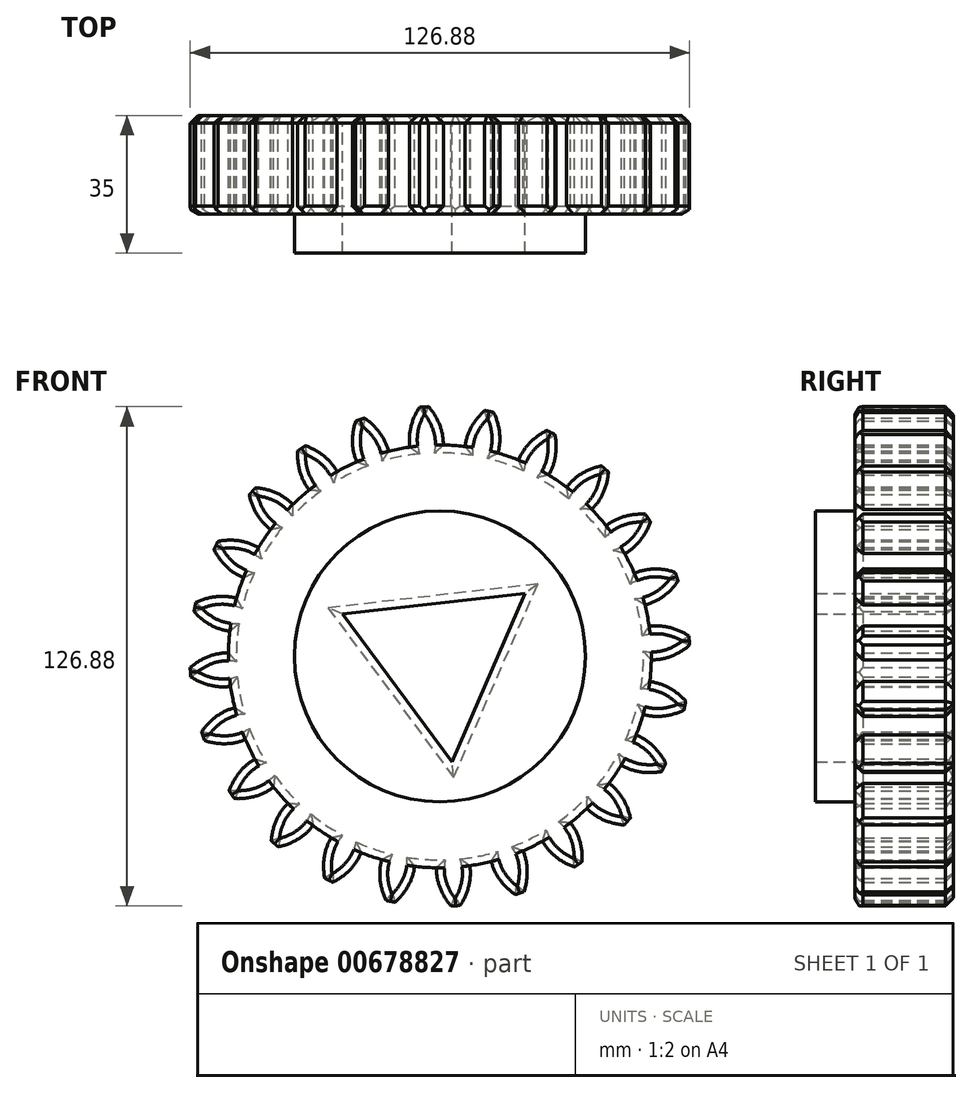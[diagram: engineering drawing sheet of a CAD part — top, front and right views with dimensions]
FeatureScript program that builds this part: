
annotation { "Feature Type Name" : "Feature", "Feature Type Description" : "" }
export const myFeature = defineFeature(function(context is Context, id is Id, definition is map)
    precondition{}
    {
        {
            var Q0;
            Q0=qCreatedBy(makeId("Front.planeOp"),FACE);
            var sketch = newSketch(context, id + "F0", { "sketchPlane" : qUnion([Q0])});
            skCircle(sketch, "E0", {"center": v(0, 0) * mm, "radius": 53.72 * mm});
            skCircle(sketch, "E1", {"center": v(0, 0) * mm, "radius": 58.67 * mm, "construction": true});
            skCircle(sketch, "E2", {"center": v(0, 0) * mm, "radius": 63.5 * mm, "construction": true});
            skLineSegment(sketch, "E3", {"start": v(0, 0) * mm, "end": v(0, 76.25) * mm, "construction": true});
            skLineSegment(sketch, "E4", {"start": v(0, 2.12) * mm, "end": v(-4.61, 72.47) * mm, "construction": true});
            skLineSegment(sketch, "E5", {"start": v(0, 58.67) * mm, "end": v(-65.77, 58.67) * mm, "construction": true});
            skLineSegment(sketch, "E6", {"start": v(0, 58.67) * mm, "end": v(-63.3, 35.64) * mm, "construction": true});
            skCircle(sketch, "E7", {"center": v(0, 58.67) * mm, "radius": 14.6 * mm, "construction": true});
            skCircle(sketch, "E8", {"center": v(-13.72, 53.68) * mm, "radius": 14.6 * mm, "construction": true});
            skArc(sketch, "E9", {"start": v(0, 58.67) * mm, "mid": v(-1.22, 61.18) * mm, "end": v(-2.86, 63.44) * mm});
            skArc(sketch, "E10", {"start": v(0.88, 53.71) * mm, "mid": v(0.68, 56.24) * mm, "end": v(0, 58.67) * mm});
            skArc(sketch, "E11.MirrorCS", {"start": v(-7.38, 58.2) * mm, "mid": v(-6.5, 60.83) * mm, "end": v(-5.17, 63.28) * mm});
            skArc(sketch, "E12.MirrorCS", {"start": v(-7.6, 53.16) * mm, "mid": v(-7.73, 55.68) * mm, "end": v(-7.38, 58.2) * mm});
            skLineSegment(sketch, "E13", {"start": v(-5.17, 63.28) * mm, "end": v(-2.86, 63.44) * mm});
            skCircle(sketch, "E14", {"center": v(0, 0) * mm, "radius": 55.14 * mm, "construction": true});
            skCircle(sketch, "E15", {"center": v(0, 0) * mm, "radius": 36.96 * mm});
            skCircle(sketch, "E16.cCircle", {"center": v(0, 0) * mm, "radius": 26.94 * mm, "construction": true});
            skLineSegment(sketch, "E16.0", {"start": v(3.04, -26.76) * mm, "end": v(-24.7, 10.75) * mm});
            skLineSegment(sketch, "E16.1", {"start": v(-24.7, 10.75) * mm, "end": v(21.66, 16.02) * mm});
            skLineSegment(sketch, "E16.2", {"start": v(21.66, 16.02) * mm, "end": v(3.04, -26.76) * mm});
            skSolve(sketch);
        }
        {
            var Q0;
            {var subQ0=sQuery(id+"F0.wireOp",EDGE,"E0");var subQ1=makeQuery(id+"F0.imprint","INTERSECT",VERTEX,{"derivedFrom":[subQ0,sQuery(id+"F0.wireOp",EDGE,"E10")]});Q0=makeQuery(id+"F0.imprint","IMPRINT",FACE,{"disambiguationData":[TD([[makeQuery(id+"F0.imprint","IMPRINT",EDGE,{"disambiguationData":[TD([[subQ1,-1.0]])],"derivedFrom":subQ0}),1.0]])]});}
            var Q1;
            Q1=makeQuery(id+"F0.imprint","IMPRINT",FACE,{"disambiguationData":[TD([[makeQuery(id+"F0.imprint","IMPRINT",EDGE,{"derivedFrom":sQuery(id+"F0.wireOp",EDGE,"E9")}),1.0]])]});
            extrude(context, id + "F1", {"entities" : qUnion([Q0, Q1]), "depth" : 25 * mm, "offsetDistance" : 25 * mm});
        }
        {
            var Q0;
            Q0=makeQuery(id+"F1.opExtrude","SWEPT_BODY",BODY,{"disambiguationData":[OSD([sQuery(id+"F0.wireOp",EDGE,"E0"),sQuery(id+"F0.wireOp",EDGE,"E9"),sQuery(id+"F0.wireOp",EDGE,"E10"),sQuery(id+"F0.wireOp",EDGE,"E11.MirrorCS"),sQuery(id+"F0.wireOp",EDGE,"E12.MirrorCS"),sQuery(id+"F0.wireOp",EDGE,"E13")])]});
            var Q1;
            Q1=makeQuery(id+"F1.opExtrude","SWEPT_FACE",FACE,{"disambiguationData":[OSD([sQuery(id+"F0.wireOp",EDGE,"E0")])]});
            circularPattern(context, id + "F2", {"entities" : qUnion([Q0]), "axis" : qUnion([Q1]), "angle" : 360 * degree, "instanceCount" : 24, "equalSpace" : true});
        }
        {
            var Q0;
            Q0=makeQuery(id+"F0.imprint","IMPRINT",FACE,{"disambiguationData":[TD([[makeQuery(id+"F0.imprint","IMPRINT",EDGE,{"derivedFrom":sQuery(id+"F0.wireOp",EDGE,"E15")}),1.0]])]});
            extrude(context, id + "F3", {"entities" : qUnion([Q0]), "operationType" : NewBodyOperationType.ADD, "depth" : 35 * mm, "offsetDistance" : 25 * mm});
        }
        {
            var Q0;
            Q0=makeQuery(id+"F2.opPattern","COPY",EDGE,{"derivedFrom":makeQuery(id+"F1.opExtrude","CAP_EDGE",EDGE,{"disambiguationData":[OSD([sQuery(id+"F0.wireOp",EDGE,"E10")])],"isStart":false}),"instanceName":"21"});
            var Q1;
            Q1=makeQuery(id+"F2.opPattern","COPY",EDGE,{"derivedFrom":makeQuery(id+"F1.opExtrude","CAP_EDGE",EDGE,{"disambiguationData":[OSD([sQuery(id+"F0.wireOp",EDGE,"E12.MirrorCS")])],"isStart":false}),"instanceName":"22"});
            var Q2;
            Q2=makeQuery(id+"F2.opPattern","COPY",EDGE,{"derivedFrom":makeQuery(id+"F1.opExtrude","CAP_EDGE",EDGE,{"disambiguationData":[OSD([sQuery(id+"F0.wireOp",EDGE,"E12.MirrorCS")])],"isStart":false}),"instanceName":"21"});
            var Q3;
            Q3=makeQuery(id+"F2.opPattern","COPY",EDGE,{"derivedFrom":makeQuery(id+"F1.opExtrude","CAP_EDGE",EDGE,{"disambiguationData":[OSD([sQuery(id+"F0.wireOp",EDGE,"E10")])],"isStart":false}),"instanceName":"22"});
            var Q4;
            Q4=makeQuery(id+"F2.opPattern","COPY",EDGE,{"derivedFrom":makeQuery(id+"F1.opExtrude","CAP_EDGE",EDGE,{"disambiguationData":[OSD([sQuery(id+"F0.wireOp",EDGE,"E12.MirrorCS")])],"isStart":false}),"instanceName":"23"});
            var Q5;
            Q5=makeQuery(id+"F2.opPattern","COPY",EDGE,{"derivedFrom":makeQuery(id+"F1.opExtrude","CAP_EDGE",EDGE,{"disambiguationData":[OSD([sQuery(id+"F0.wireOp",EDGE,"E10")])],"isStart":false}),"instanceName":"23"});
            var Q6;
            Q6=makeQuery(id+"F1.opExtrude","CAP_EDGE",EDGE,{"disambiguationData":[OSD([sQuery(id+"F0.wireOp",EDGE,"E12.MirrorCS")])],"isStart":false});
            var Q7;
            Q7=makeQuery(id+"F1.opExtrude","CAP_EDGE",EDGE,{"disambiguationData":[OSD([sQuery(id+"F0.wireOp",EDGE,"E10")])],"isStart":false});
            var Q8;
            Q8=makeQuery(id+"F2.opPattern","COPY",EDGE,{"derivedFrom":makeQuery(id+"F1.opExtrude","CAP_EDGE",EDGE,{"disambiguationData":[OSD([sQuery(id+"F0.wireOp",EDGE,"E12.MirrorCS")])],"isStart":false}),"instanceName":"1"});
            var Q9;
            Q9=makeQuery(id+"F2.opPattern","COPY",EDGE,{"derivedFrom":makeQuery(id+"F1.opExtrude","CAP_EDGE",EDGE,{"disambiguationData":[OSD([sQuery(id+"F0.wireOp",EDGE,"E10")])],"isStart":false}),"instanceName":"1"});
            var Q10;
            Q10=makeQuery(id+"F2.opPattern","COPY",EDGE,{"derivedFrom":makeQuery(id+"F1.opExtrude","CAP_EDGE",EDGE,{"disambiguationData":[OSD([sQuery(id+"F0.wireOp",EDGE,"E12.MirrorCS")])],"isStart":false}),"instanceName":"2"});
            var Q11;
            Q11=makeQuery(id+"F2.opPattern","COPY",EDGE,{"derivedFrom":makeQuery(id+"F1.opExtrude","CAP_EDGE",EDGE,{"disambiguationData":[OSD([sQuery(id+"F0.wireOp",EDGE,"E10")])],"isStart":false}),"instanceName":"2"});
            var Q12;
            Q12=makeQuery(id+"F2.opPattern","COPY",EDGE,{"derivedFrom":makeQuery(id+"F1.opExtrude","CAP_EDGE",EDGE,{"disambiguationData":[OSD([sQuery(id+"F0.wireOp",EDGE,"E12.MirrorCS")])],"isStart":false}),"instanceName":"3"});
            var Q13;
            Q13=makeQuery(id+"F2.opPattern","COPY",EDGE,{"derivedFrom":makeQuery(id+"F1.opExtrude","CAP_EDGE",EDGE,{"disambiguationData":[OSD([sQuery(id+"F0.wireOp",EDGE,"E10")])],"isStart":false}),"instanceName":"3"});
            var Q14;
            Q14=makeQuery(id+"F2.opPattern","COPY",EDGE,{"derivedFrom":makeQuery(id+"F1.opExtrude","CAP_EDGE",EDGE,{"disambiguationData":[OSD([sQuery(id+"F0.wireOp",EDGE,"E12.MirrorCS")])],"isStart":false}),"instanceName":"4"});
            var Q15;
            Q15=makeQuery(id+"F2.opPattern","COPY",EDGE,{"derivedFrom":makeQuery(id+"F1.opExtrude","CAP_EDGE",EDGE,{"disambiguationData":[OSD([sQuery(id+"F0.wireOp",EDGE,"E10")])],"isStart":false}),"instanceName":"4"});
            var Q16;
            Q16=makeQuery(id+"F2.opPattern","COPY",EDGE,{"derivedFrom":makeQuery(id+"F1.opExtrude","CAP_EDGE",EDGE,{"disambiguationData":[OSD([sQuery(id+"F0.wireOp",EDGE,"E10")])],"isStart":false}),"instanceName":"5"});
            var Q17;
            Q17=makeQuery(id+"F2.opPattern","COPY",EDGE,{"derivedFrom":makeQuery(id+"F1.opExtrude","CAP_EDGE",EDGE,{"disambiguationData":[OSD([sQuery(id+"F0.wireOp",EDGE,"E12.MirrorCS")])],"isStart":false}),"instanceName":"5"});
            var Q18;
            Q18=makeQuery(id+"F2.opPattern","COPY",EDGE,{"derivedFrom":makeQuery(id+"F1.opExtrude","CAP_EDGE",EDGE,{"disambiguationData":[OSD([sQuery(id+"F0.wireOp",EDGE,"E12.MirrorCS")])],"isStart":false}),"instanceName":"6"});
            var Q19;
            Q19=makeQuery(id+"F2.opPattern","COPY",EDGE,{"derivedFrom":makeQuery(id+"F1.opExtrude","CAP_EDGE",EDGE,{"disambiguationData":[OSD([sQuery(id+"F0.wireOp",EDGE,"E10")])],"isStart":false}),"instanceName":"6"});
            var Q20;
            Q20=makeQuery(id+"F2.opPattern","COPY",EDGE,{"derivedFrom":makeQuery(id+"F1.opExtrude","CAP_EDGE",EDGE,{"disambiguationData":[OSD([sQuery(id+"F0.wireOp",EDGE,"E12.MirrorCS")])],"isStart":false}),"instanceName":"7"});
            var Q21;
            Q21=makeQuery(id+"F2.opPattern","COPY",EDGE,{"derivedFrom":makeQuery(id+"F1.opExtrude","CAP_EDGE",EDGE,{"disambiguationData":[OSD([sQuery(id+"F0.wireOp",EDGE,"E10")])],"isStart":false}),"instanceName":"7"});
            var Q22;
            Q22=makeQuery(id+"F2.opPattern","COPY",EDGE,{"derivedFrom":makeQuery(id+"F1.opExtrude","CAP_EDGE",EDGE,{"disambiguationData":[OSD([sQuery(id+"F0.wireOp",EDGE,"E12.MirrorCS")])],"isStart":false}),"instanceName":"8"});
            var Q23;
            Q23=makeQuery(id+"F2.opPattern","COPY",EDGE,{"derivedFrom":makeQuery(id+"F1.opExtrude","CAP_EDGE",EDGE,{"disambiguationData":[OSD([sQuery(id+"F0.wireOp",EDGE,"E10")])],"isStart":false}),"instanceName":"8"});
            var Q24;
            Q24=makeQuery(id+"F2.opPattern","COPY",EDGE,{"derivedFrom":makeQuery(id+"F1.opExtrude","CAP_EDGE",EDGE,{"disambiguationData":[OSD([sQuery(id+"F0.wireOp",EDGE,"E12.MirrorCS")])],"isStart":false}),"instanceName":"9"});
            var Q25;
            Q25=makeQuery(id+"F2.opPattern","COPY",EDGE,{"derivedFrom":makeQuery(id+"F1.opExtrude","CAP_EDGE",EDGE,{"disambiguationData":[OSD([sQuery(id+"F0.wireOp",EDGE,"E10")])],"isStart":false}),"instanceName":"9"});
            var Q26;
            Q26=makeQuery(id+"F2.opPattern","COPY",EDGE,{"derivedFrom":makeQuery(id+"F1.opExtrude","CAP_EDGE",EDGE,{"disambiguationData":[OSD([sQuery(id+"F0.wireOp",EDGE,"E12.MirrorCS")])],"isStart":false}),"instanceName":"10"});
            var Q27;
            Q27=makeQuery(id+"F2.opPattern","COPY",EDGE,{"derivedFrom":makeQuery(id+"F1.opExtrude","CAP_EDGE",EDGE,{"disambiguationData":[OSD([sQuery(id+"F0.wireOp",EDGE,"E10")])],"isStart":false}),"instanceName":"10"});
            var Q28;
            Q28=makeQuery(id+"F2.opPattern","COPY",EDGE,{"derivedFrom":makeQuery(id+"F1.opExtrude","CAP_EDGE",EDGE,{"disambiguationData":[OSD([sQuery(id+"F0.wireOp",EDGE,"E12.MirrorCS")])],"isStart":false}),"instanceName":"11"});
            var Q29;
            Q29=makeQuery(id+"F2.opPattern","COPY",EDGE,{"derivedFrom":makeQuery(id+"F1.opExtrude","CAP_EDGE",EDGE,{"disambiguationData":[OSD([sQuery(id+"F0.wireOp",EDGE,"E10")])],"isStart":false}),"instanceName":"11"});
            var Q30;
            Q30=makeQuery(id+"F2.opPattern","COPY",EDGE,{"derivedFrom":makeQuery(id+"F1.opExtrude","CAP_EDGE",EDGE,{"disambiguationData":[OSD([sQuery(id+"F0.wireOp",EDGE,"E12.MirrorCS")])],"isStart":false}),"instanceName":"12"});
            var Q31;
            Q31=makeQuery(id+"F2.opPattern","COPY",EDGE,{"derivedFrom":makeQuery(id+"F1.opExtrude","CAP_EDGE",EDGE,{"disambiguationData":[OSD([sQuery(id+"F0.wireOp",EDGE,"E10")])],"isStart":false}),"instanceName":"12"});
            var Q32;
            Q32=makeQuery(id+"F2.opPattern","COPY",EDGE,{"derivedFrom":makeQuery(id+"F1.opExtrude","CAP_EDGE",EDGE,{"disambiguationData":[OSD([sQuery(id+"F0.wireOp",EDGE,"E12.MirrorCS")])],"isStart":false}),"instanceName":"13"});
            var Q33;
            Q33=makeQuery(id+"F2.opPattern","COPY",EDGE,{"derivedFrom":makeQuery(id+"F1.opExtrude","CAP_EDGE",EDGE,{"disambiguationData":[OSD([sQuery(id+"F0.wireOp",EDGE,"E10")])],"isStart":false}),"instanceName":"13"});
            var Q34;
            Q34=makeQuery(id+"F2.opPattern","COPY",EDGE,{"derivedFrom":makeQuery(id+"F1.opExtrude","CAP_EDGE",EDGE,{"disambiguationData":[OSD([sQuery(id+"F0.wireOp",EDGE,"E12.MirrorCS")])],"isStart":false}),"instanceName":"14"});
            var Q35;
            Q35=makeQuery(id+"F2.opPattern","COPY",EDGE,{"derivedFrom":makeQuery(id+"F1.opExtrude","CAP_EDGE",EDGE,{"disambiguationData":[OSD([sQuery(id+"F0.wireOp",EDGE,"E10")])],"isStart":false}),"instanceName":"14"});
            var Q36;
            Q36=makeQuery(id+"F2.opPattern","COPY",EDGE,{"derivedFrom":makeQuery(id+"F1.opExtrude","CAP_EDGE",EDGE,{"disambiguationData":[OSD([sQuery(id+"F0.wireOp",EDGE,"E12.MirrorCS")])],"isStart":false}),"instanceName":"15"});
            var Q37;
            Q37=makeQuery(id+"F2.opPattern","COPY",EDGE,{"derivedFrom":makeQuery(id+"F1.opExtrude","CAP_EDGE",EDGE,{"disambiguationData":[OSD([sQuery(id+"F0.wireOp",EDGE,"E10")])],"isStart":false}),"instanceName":"15"});
            var Q38;
            Q38=makeQuery(id+"F2.opPattern","COPY",EDGE,{"derivedFrom":makeQuery(id+"F1.opExtrude","CAP_EDGE",EDGE,{"disambiguationData":[OSD([sQuery(id+"F0.wireOp",EDGE,"E10")])],"isStart":false}),"instanceName":"16"});
            var Q39;
            Q39=makeQuery(id+"F2.opPattern","COPY",EDGE,{"derivedFrom":makeQuery(id+"F1.opExtrude","CAP_EDGE",EDGE,{"disambiguationData":[OSD([sQuery(id+"F0.wireOp",EDGE,"E12.MirrorCS")])],"isStart":false}),"instanceName":"16"});
            var Q40;
            Q40=makeQuery(id+"F2.opPattern","COPY",EDGE,{"derivedFrom":makeQuery(id+"F1.opExtrude","CAP_EDGE",EDGE,{"disambiguationData":[OSD([sQuery(id+"F0.wireOp",EDGE,"E12.MirrorCS")])],"isStart":false}),"instanceName":"17"});
            var Q41;
            Q41=makeQuery(id+"F2.opPattern","COPY",EDGE,{"derivedFrom":makeQuery(id+"F1.opExtrude","CAP_EDGE",EDGE,{"disambiguationData":[OSD([sQuery(id+"F0.wireOp",EDGE,"E10")])],"isStart":false}),"instanceName":"17"});
            var Q42;
            Q42=makeQuery(id+"F2.opPattern","COPY",EDGE,{"derivedFrom":makeQuery(id+"F1.opExtrude","CAP_EDGE",EDGE,{"disambiguationData":[OSD([sQuery(id+"F0.wireOp",EDGE,"E12.MirrorCS")])],"isStart":false}),"instanceName":"18"});
            var Q43;
            Q43=makeQuery(id+"F2.opPattern","COPY",EDGE,{"derivedFrom":makeQuery(id+"F1.opExtrude","CAP_EDGE",EDGE,{"disambiguationData":[OSD([sQuery(id+"F0.wireOp",EDGE,"E10")])],"isStart":false}),"instanceName":"18"});
            var Q44;
            Q44=makeQuery(id+"F2.opPattern","COPY",EDGE,{"derivedFrom":makeQuery(id+"F1.opExtrude","CAP_EDGE",EDGE,{"disambiguationData":[OSD([sQuery(id+"F0.wireOp",EDGE,"E12.MirrorCS")])],"isStart":false}),"instanceName":"19"});
            var Q45;
            Q45=makeQuery(id+"F2.opPattern","COPY",EDGE,{"derivedFrom":makeQuery(id+"F1.opExtrude","CAP_EDGE",EDGE,{"disambiguationData":[OSD([sQuery(id+"F0.wireOp",EDGE,"E10")])],"isStart":false}),"instanceName":"19"});
            var Q46;
            Q46=makeQuery(id+"F2.opPattern","COPY",EDGE,{"derivedFrom":makeQuery(id+"F1.opExtrude","CAP_EDGE",EDGE,{"disambiguationData":[OSD([sQuery(id+"F0.wireOp",EDGE,"E12.MirrorCS")])],"isStart":false}),"instanceName":"20"});
            var Q47;
            Q47=makeQuery(id+"F2.opPattern","COPY",EDGE,{"derivedFrom":makeQuery(id+"F1.opExtrude","CAP_EDGE",EDGE,{"disambiguationData":[OSD([sQuery(id+"F0.wireOp",EDGE,"E10")])],"isStart":false}),"instanceName":"20"});
            var Q48;
            {var subQ0=sQuery(id+"F0.wireOp",EDGE,"E15");var subQ1=makeQuery(id+"F1.opExtrude","CAP_FACE",FACE,{"disambiguationData":[OSD([sQuery(id+"F0.wireOp",EDGE,"E0"),sQuery(id+"F0.wireOp",EDGE,"E9"),sQuery(id+"F0.wireOp",EDGE,"E10"),sQuery(id+"F0.wireOp",EDGE,"E11.MirrorCS"),sQuery(id+"F0.wireOp",EDGE,"E12.MirrorCS"),sQuery(id+"F0.wireOp",EDGE,"E13"),subQ0])],"isStart":true});Q48=makeQuery(id+"F3.boolean.opBoolean","MERGE",FACE,{"derivedFrom":[subQ1,makeQuery(id+"F2.opPattern","COPY",FACE,{"derivedFrom":subQ1,"instanceName":"1"}),makeQuery(id+"F2.opPattern","COPY",FACE,{"derivedFrom":subQ1,"instanceName":"2"}),makeQuery(id+"F2.opPattern","COPY",FACE,{"derivedFrom":subQ1,"instanceName":"3"}),makeQuery(id+"F2.opPattern","COPY",FACE,{"derivedFrom":subQ1,"instanceName":"4"}),makeQuery(id+"F2.opPattern","COPY",FACE,{"derivedFrom":subQ1,"instanceName":"5"}),makeQuery(id+"F2.opPattern","COPY",FACE,{"derivedFrom":subQ1,"instanceName":"6"}),makeQuery(id+"F2.opPattern","COPY",FACE,{"derivedFrom":subQ1,"instanceName":"7"}),makeQuery(id+"F2.opPattern","COPY",FACE,{"derivedFrom":subQ1,"instanceName":"8"}),makeQuery(id+"F2.opPattern","COPY",FACE,{"derivedFrom":subQ1,"instanceName":"9"}),makeQuery(id+"F2.opPattern","COPY",FACE,{"derivedFrom":subQ1,"instanceName":"10"}),makeQuery(id+"F2.opPattern","COPY",FACE,{"derivedFrom":subQ1,"instanceName":"11"}),makeQuery(id+"F2.opPattern","COPY",FACE,{"derivedFrom":subQ1,"instanceName":"12"}),makeQuery(id+"F2.opPattern","COPY",FACE,{"derivedFrom":subQ1,"instanceName":"13"}),makeQuery(id+"F2.opPattern","COPY",FACE,{"derivedFrom":subQ1,"instanceName":"14"}),makeQuery(id+"F2.opPattern","COPY",FACE,{"derivedFrom":subQ1,"instanceName":"15"}),makeQuery(id+"F2.opPattern","COPY",FACE,{"derivedFrom":subQ1,"instanceName":"16"}),makeQuery(id+"F2.opPattern","COPY",FACE,{"derivedFrom":subQ1,"instanceName":"17"}),makeQuery(id+"F2.opPattern","COPY",FACE,{"derivedFrom":subQ1,"instanceName":"18"}),makeQuery(id+"F2.opPattern","COPY",FACE,{"derivedFrom":subQ1,"instanceName":"19"}),makeQuery(id+"F2.opPattern","COPY",FACE,{"derivedFrom":subQ1,"instanceName":"20"}),makeQuery(id+"F2.opPattern","COPY",FACE,{"derivedFrom":subQ1,"instanceName":"21"}),makeQuery(id+"F2.opPattern","COPY",FACE,{"derivedFrom":subQ1,"instanceName":"22"}),makeQuery(id+"F2.opPattern","COPY",FACE,{"derivedFrom":subQ1,"instanceName":"23"}),makeQuery(id+"F3.opExtrude","CAP_FACE",FACE,{"disambiguationData":[OSD([subQ0,sQuery(id+"F0.wireOp",EDGE,"E16.0"),sQuery(id+"F0.wireOp",EDGE,"E16.1"),sQuery(id+"F0.wireOp",EDGE,"E16.2")])],"isStart":true})]});}
            chamfer(context, id + "F4", {"entities" : qUnion([Q0, Q1, Q2, Q3, Q4, Q5, Q6, Q7, Q8, Q9, Q10, Q11, Q12, Q13, Q14, Q15, Q16, Q17, Q18, Q19, Q20, Q21, Q22, Q23, Q24, Q25, Q26, Q27, Q28, Q29, Q30, Q31, Q32, Q33, Q34, Q35, Q36, Q37, Q38, Q39, Q40, Q41, Q42, Q43, Q44, Q45, Q46, Q47, Q48]), "width" : 2 * mm, "tangentPropagation" : true});
        }
    });
